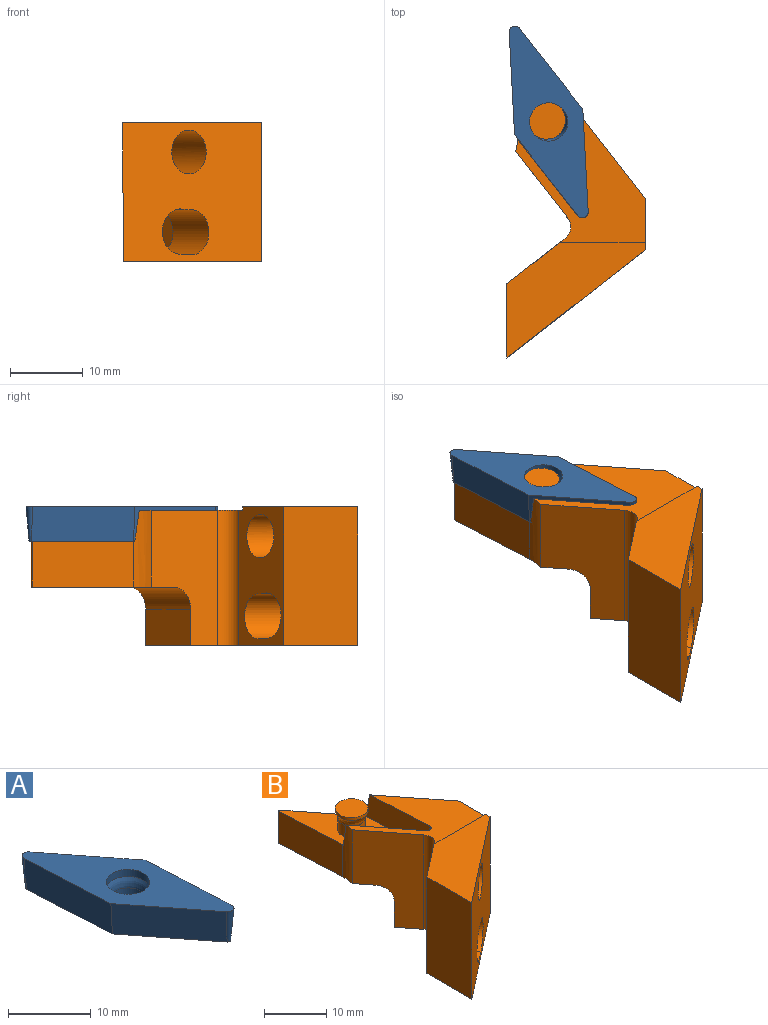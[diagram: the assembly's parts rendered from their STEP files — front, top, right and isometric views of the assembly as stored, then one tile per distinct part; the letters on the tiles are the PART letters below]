
ASSEMBLY  parts=2 mates=1
PART A: 11 faces, bbox 10.8x26.3x4.8 mm
  f0: cone r=0.38mm half-angle=5deg, axis (0,0,1), area 7.1mm2, adj f1,f5,f6,f7
  f1: plane 14.09x4.76mm, normal (-0.99,-0.05,-0.09), area 67mm2, adj f0,f2,f6,f7
  f2: plane 11.25x9mm, normal (-0.79,-0.61,-0.09), area 67mm2, adj f1,f3,f6,f7
  f3: cone r=0.38mm half-angle=5deg, axis (0,0,1), area 7.1mm2, adj f2,f4,f6,f7
  f4: plane 14.09x4.76mm, normal (0.99,0.05,-0.09), area 67mm2, adj f3,f5,f6,f7
  f5: plane 11.25x9mm, normal (0.79,0.61,-0.09), area 67mm2, adj f0,f4,f6,f7
  f6: plane 26.31x10.83mm, normal (0,0,1), area 134.1mm2, adj f0,f1,f2,f3,f4,f5,f8
  f7: plane 25.48x10mm, normal (0,0,-1), area 116mm2, adj f0,f1,f2,f3,f4,f5,f10
  f8: cylinder r=2.62mm len=5.25mm, axis (0,0,-1), area 17.4mm2, adj f6,f9
  f9: torus R=4.7mm, axis (0,0,-1), area 21.8mm2, adj f8,f10
  f10: cylinder r=2.2mm len=4.4mm, axis (0,0,-1), area 31.9mm2, adj f7,f9
PART B: 30 faces, bbox 19x44.8x19 mm
  f0: plane 19x15.79mm, normal (0,0,1), area 138.6mm2, adj f1,f2,f9,f18,f19
  f1: plane 19x10.22mm, normal (-1,0,0), area 192.9mm2, adj f0,f3,f18,f19
  f2: plane 19x7mm, normal (1,0,0), area 130.2mm2, adj f0,f3,f9,f14,f15,f18
  f3: plane 29.04x18.92mm, normal (0,0,-1), area 257.8mm2, adj f1,f2,f15,f18,f19,f20,f28,f29
  f4: plane 5.25x5.25mm, normal (0,0,1), area 21.6mm2, adj f5
  f5: cylinder r=2.62mm len=5.25mm, axis (0,0,-1), area 9mm2, adj f4,f6
  f6: revolved ~5.24x5.24mm, area 21.8mm2, adj f5,f7
  f7: cylinder r=2.2mm len=4.4mm, axis (0,0,-1), area 31.9mm2, adj f6,f11
  f8: cone r=0.75mm half-angle=5deg, axis (0,0,1), area 6.1mm2, adj f10,f11,f13,f14
  f9: plane 11.79x0.46mm, normal (0,1,0), area 5.4mm2, adj f0,f2,f14,f19
  f10: plane 13.44x4.25mm, normal (-0.99,-0.05,0.09), area 56.3mm2, adj f8,f11,f14,f15
  f11: plane 24.89x9.66mm, normal (0,0,1), area 107.1mm2, adj f7,f8,f10,f12,f13,f15,f16,f17
  f12: plane 6.29x0.32mm, normal (-0.35,0.94,0), area 2.1mm2, adj f11,f15,f16,f26
  f13: plane 10.78x8.25mm, normal (0.79,0.61,0.09), area 56.1mm2, adj f8,f11,f14,f17
  f14: plane 17.76x17.44mm, normal (0,0,1), area 120.9mm2, adj f2,f8,f9,f10,f13,f15,f17,f19
  f15: plane 22.94x18.54mm, normal (0.79,0.62,0), area 321.5mm2, adj f2,f3,f10,f11,f12,f14,f26,f27
  f16: plane 13.88x6.29mm, normal (-1,-0.05,0), area 87.4mm2, adj f11,f12,f17,f26
  f17: cylinder r=8.1mm len=10.54mm, axis (0,0,1), area 24mm2, adj f11,f13,f14,f16,f20,f26
  f18: plane 19x19mm, normal (0.62,-0.79,0), area 386.7mm2, adj f0,f1,f2,f3,f21,f22,f23,f24
  f19: plane 19x8.01mm, normal (-0.62,0.79,0), area 121.4mm2, adj f0,f1,f3,f9,f14,f21,f22,f23
  f20: plane 18.54x9.11mm, normal (-0.79,-0.62,0), area 161.7mm2, adj f3,f14,f17,f26,f27,f28,f29
  f21: cylinder r=3mm len=10mm, axis (-0.62,0.79,0), area 150.8mm2, adj f18,f19
  f22: cylinder r=3.1mm len=8.48mm, axis (0.62,-0.79,0), area 77.9mm2, adj f18,f19,f23,f25
  f23: cylinder r=7.9mm len=7.15mm, axis (0.62,-0.79,0), area 11mm2, adj f18,f19,f22,f24
  f24: cylinder r=3.1mm len=8.28mm, axis (0.62,-0.79,0), area 77.9mm2, adj f18,f19,f23,f25
  f25: cylinder r=14.1mm len=7.82mm, axis (0.62,-0.79,0), area 19.7mm2, adj f18,f19,f22,f24
  f26: plane 19.47x10.72mm, normal (0,0,-1), area 103.5mm2, adj f12,f15,f16,f17,f20,f27
  f27: cylinder r=3mm len=9.73mm, axis (-0.79,-0.62,0), area 47.1mm2, adj f15,f20,f26,f28
  f28: plane 7.88x6.16mm, normal (-0.62,0.79,0), area 50mm2, adj f3,f15,f20,f27
  f29: cylinder r=2mm len=18.54mm, axis (0,0,1), area 58.2mm2, adj f3,f14,f19,f20
PLACE A t=(7.28,-10.65,-5.68)mm
PLACE B t=(6.94,-10.37,-5.68)mm
MATE fastened B.f11 <-> A.f7  axis (0,0,1) through (-10.99,108.57,8.61)mm
